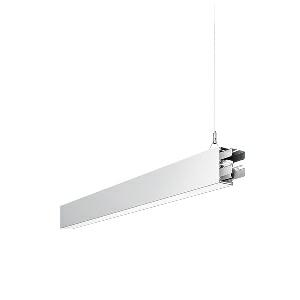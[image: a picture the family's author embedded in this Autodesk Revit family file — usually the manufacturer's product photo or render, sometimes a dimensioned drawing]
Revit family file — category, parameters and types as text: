
# Revit family: idoo_line_-_ilp_3000_840_d_mid_00805689_7bc0
name_source: partatom
category: Lighting Fixtures
units: mm (PartAtom-declared; Revit-internal decimal feet)

## family parameters
Cut with Voids When Loaded = No
Host = Face
Light Source = No
Part Type = Normal
Room Calculation Point = No
Round Connector Dimension = Use Diameter
Shared = No

## types (1)
- IDOO.line - ILP 3000/840/D MID (1 x LED, 3150 lm, 4000K)
    Apparent Load = 23 VA
    Approval mark = CE
    CIE Flux Codes = 66 91 98 40 100
    Color Rendering = 80-89
    Color Temperature = 4000K
    Control Gear = Electronic ballast
    Default Elevation = 1800 mm
    Description = ILP 3000/840/D|Suspended luminaire|light source: LED|connected load: 220-240 V, 50/60 Hz|Power consumption: approx. 23 W|standby: approx. 0,20|luminous flux: 3150 lm|luminous efficacy: 136 lm/W|light distribution: Direct/indirect|direct ratio: approx. 40 %|colour temperature: Cold white, ca. 4000 K|color rendering index (CRI): >= 80|chromaticity tolerance:  3 SDCM|System of protection: IP 40|technology: Continuously dimmable|luminaire body|material: Sectional aluminium|colour: White|lamp cover: Acrylic (PMMA), Clear|mains lead: 1,0 m With free stranded wires|Fastening: Steel cable 0.3 - 0.7 m|glare control: Prism aperture|luminance(L65): <= 2700 cd/m|unified glare rating(4H 8H): <=  16|special features: DALI Load 1x, TouchDIM - dimming via standard switch, Through-wired, up to 18 m on one mains connection, Flicker-free, Suitable as emergency lighting, Mechanical and electrical connection of the individual modules without tools|
    Frequency = 50 Hz
    Height = 110 mm
    Lamp = 1 x LED
    Lamp Light Flux = 3150 lm
    Lamp count = 1
    Length = 1122 mm
    Luminous efficacy = 137 lm/W
    Manufacturer = Waldmann
    ModVariant = No
    Model = 00805689
    Mounting Place = Ceiling
    Mounting Type = Pendant
    Number of Poles = 1
    OnlyDefault = Yes
    Power Factor = 1
    Product Name = IDOO.line - ILP 3000/840/D MID
    Product group = Suspended luminaire
    ProductGroupID = 9
    Protection Class = Protection class I
    Protection Degree = IP 40
    RLX_Detail_Level = 1
    RLX_Emergency_Light_Flux = 0 lm
    RLX_Emergency_Type = 0
    RLX_Emergency_Type_DB = No
    RlxData = <blob elided: 19309 chars, md5=f3d05b3f>
    Socket = socket
    Standby Power = 0 W
    System Light Flux = 3150 lm
    System Power = 23 W
    Type Comments = Product without accessories
    Type Image = 113302000-00692570.jpg
    URL = http://relux.com
    VarID = ---
    Voltage = 230 V
    Voltage Range = 220-240 V
    Weight = 0.00 kg
    Width = 60 mm  [stored 0.19685 ft]

note: [stored X ft] marks values corroborated as IEEE doubles in the binary element streams (Revit-internal decimal feet)

## geometry (parser evidence)
native form markers: Blend x4, Sweep x13
no freeform markers — native parametric forms only
